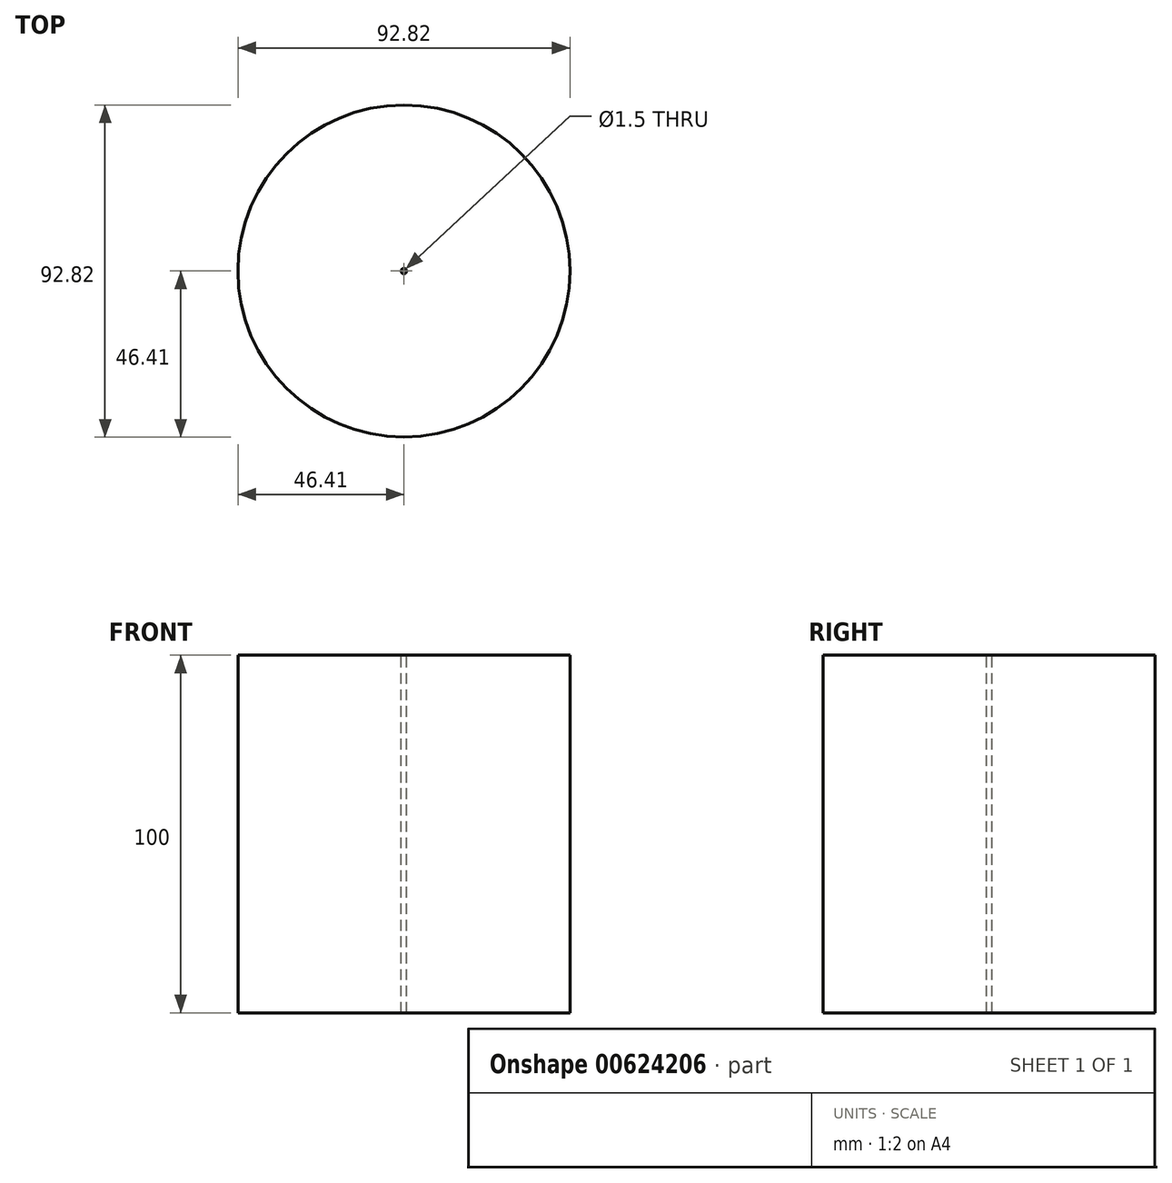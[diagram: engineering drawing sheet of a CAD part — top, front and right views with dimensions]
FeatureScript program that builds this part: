
annotation { "Feature Type Name" : "Feature", "Feature Type Description" : "" }
export const myFeature = defineFeature(function(context is Context, id is Id, definition is map)
    precondition{}
    {
        {
            var Q0;
            Q0=qCreatedBy(makeId("Top.planeOp"),FACE);
            var sketch = newSketch(context, id + "F0", { "sketchPlane" : qUnion([Q0])});
            skCircle(sketch, "E0", {"center": v(0, 0) * mm, "radius": 46.41 * mm});
            skSolve(sketch);
        }
        {
            var Q0;
            Q0 = qSketchRegion(id + "F0", true);
            extrude(context, id + "F1", {"entities" : qUnion([Q0]), "depth" : 100 * mm, "offsetDistance" : 25 * mm});
        }
        {
            var Q0;
            Q0=makeQuery(id+"F1.opExtrude","CAP_FACE",FACE,{"disambiguationData":[OSD([sQuery(id+"F0.wireOp",EDGE,"E0")])],"isStart":false});
            cPlane(context, id + "F2", {"entities" : qUnion([Q0]), "cplaneType" : CPlaneType.OFFSET, "offset" : 0 * mm, "width" : 150 * mm, "height" : 150 * mm});
        }
        {
            var Q0;
            Q0=qCreatedBy(id+"F2.planeOp",FACE);
            var sketch = newSketch(context, id + "F3", { "sketchPlane" : qUnion([Q0])});
            skCircle(sketch, "E1", {"center": v(0, 0) * mm, "radius": 0.75 * mm});
            skSolve(sketch);
        }
        {
            var Q0;
            Q0=makeQuery(id+"F3.imprint","IMPRINT",FACE,{"disambiguationData":[TD([[makeQuery(id+"F3.imprint","IMPRINT",EDGE,{"derivedFrom":sQuery(id+"F3.wireOp",EDGE,"E1")}),1.0]])]});
            extrude(context, id + "F4", {"entities" : qUnion([Q0]), "operationType" : NewBodyOperationType.REMOVE, "endBound" : BoundingType.THROUGH_ALL, "oppositeDirection" : true, "depth" : 25 * mm, "offsetDistance" : 25 * mm});
        }
    });
